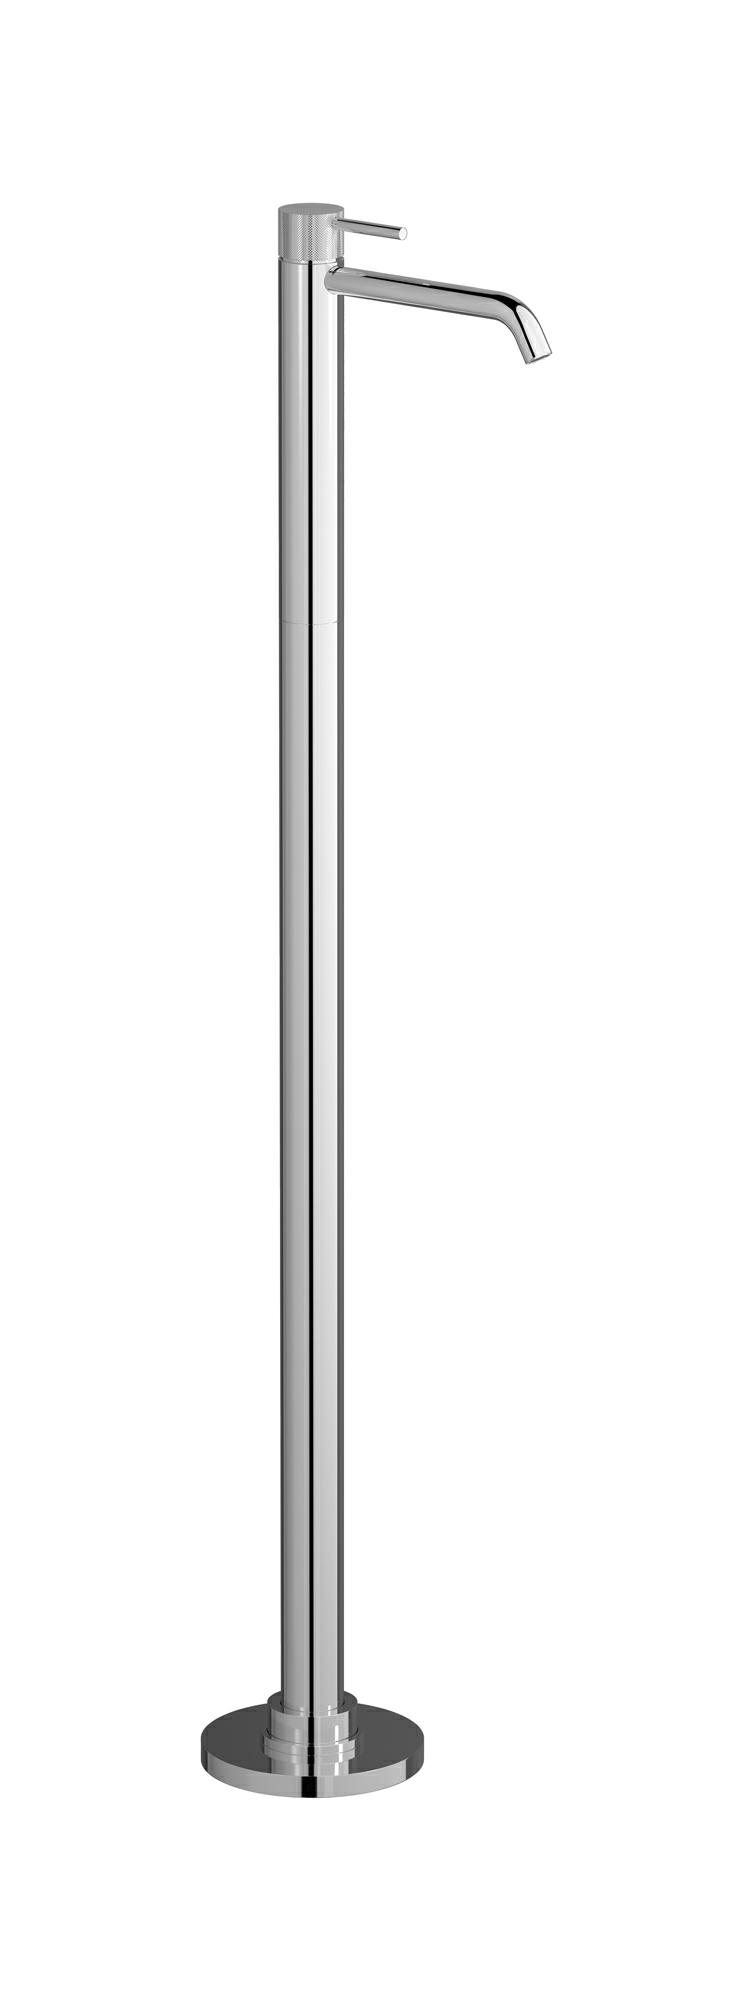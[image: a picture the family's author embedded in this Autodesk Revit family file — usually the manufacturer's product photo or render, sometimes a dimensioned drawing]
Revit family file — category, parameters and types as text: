
# Revit family: ID299
name_source: partatom
category: Apparecchi idraulici
units: mm (PartAtom-declared; Revit-internal decimal feet)

## family parameters
Basato su piano di lavoro = No
Condiviso = No
Mantieni orientamento annotazione = No
Numero OmniClass = 23.45.55.17
Punto di calcolo locali = No
Quota connettore circolare = Usa diametro
Sempre verticale = Sì
Taglio con vuoti quando caricato = No
Tipo di parte = Normale
Titolo OmniClass = Mixing Faucets

## types (12) — shared parameters
Cold water inlet = 10 mm  [stored 0.0328084 ft]
Commenti sul tipo = Washbasin mixer
Connessione CW = No
Connessione HW = No
Connessione di scarico = No
Connessione di ventilazione = No
Descrizione = Monohole freestanding washbasin mixer complete with drain
Hot water inlet = 10 mm  [stored 0.0328084 ft]
Produttore = IB Rubinetterie S.p.A.
URL = https://www.weareib.it
zero-valued in all types: Prospetto di default

## per-type parameters (varying)
| type | Finishes surface | Immagine tipo | Modello |
| Chrome | IB_Chrome | ID299CC.jpg | ID299CC |
| Brushed nickel | IB_Brushed nickel | ID299SS.jpg | ID299SS |
| Natural brass | IB_Brass | ID299ON.jpg | ID299ON |
| Matt black | IB_matt black | ID299NP.jpg | ID299NP |
| Black chrome | IB_Black chrome | ID299CF.jpg | ID299CF |
| Brushed black chrome | IB_Brushed black chrome | ID299CS.jpg | ID299CS |
| Pale gold | IB_Pale gold | ID299II.jpg | ID299II |
| Brushed pale gold | IB_brushed pale gold | ID299IS.jpg | ID299IS |
| Rose gold | IB_Rose gold | ID299RS.jpg | ID299RS |
| Brushed rose gold | IB_Brushed rose gold | ID299SR.jpg | ID299SR |
| Gold | IB_gold | ID299OO.jpg | ID299OO |
| Brushed gold | IB_brushed gold | ID299OS.jpg | ID299OS |

note: [stored X ft] marks values corroborated as IEEE doubles in the binary element streams (Revit-internal decimal feet)
